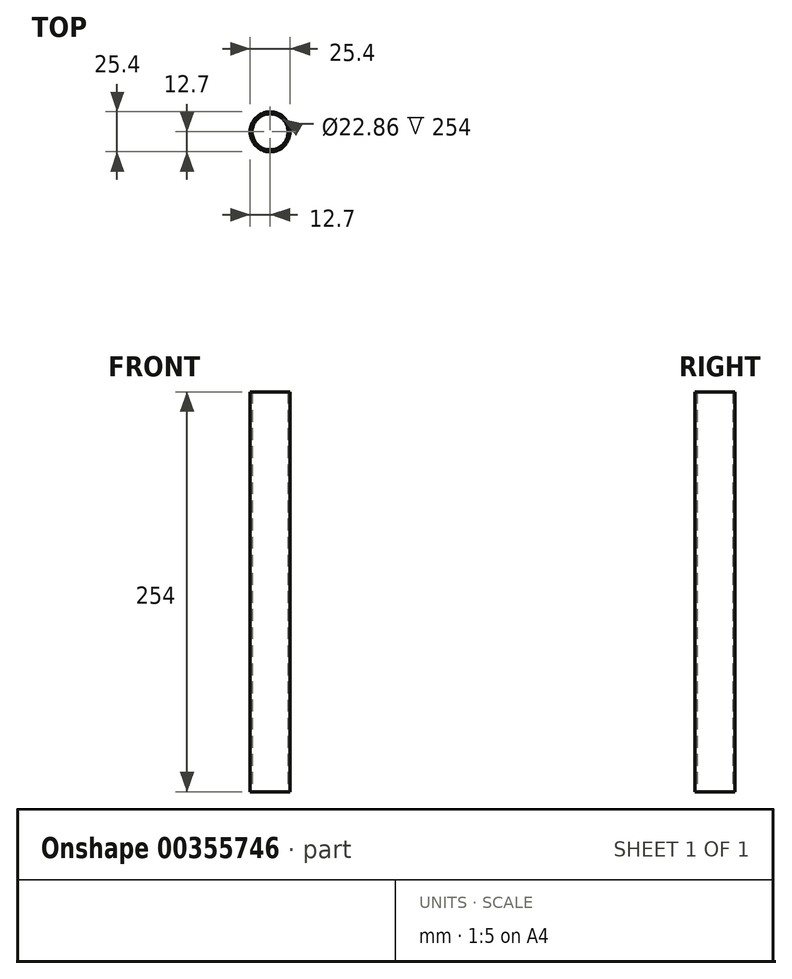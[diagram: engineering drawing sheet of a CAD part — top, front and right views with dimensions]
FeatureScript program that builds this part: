
annotation { "Feature Type Name" : "Feature", "Feature Type Description" : "" }
export const myFeature = defineFeature(function(context is Context, id is Id, definition is map)
    precondition{}
    {
        {
            var Q0;
            Q0=qCreatedBy(makeId("Top.planeOp"),FACE);
            var sketch = newSketch(context, id + "F0", { "sketchPlane" : qUnion([Q0])});
            skCircle(sketch, "E0", {"center": v(0, 0) * mm, "radius": 11.43 * mm});
            skCircle(sketch, "E1", {"center": v(0, 0) * mm, "radius": 12.7 * mm});
            skSolve(sketch);
        }
        {
            var Q0;
            Q0=qSketchRegion(id+"F0",true);
            extrude(context, id + "F1", {"entities" : qUnion([Q0]), "depth" : 254 * mm});
        }
    });
